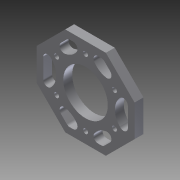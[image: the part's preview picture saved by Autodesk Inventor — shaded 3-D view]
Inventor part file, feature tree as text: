
AUTODESK INVENTOR PART (.ipt)
format: ipt  version: 2012 (Build 160160000, 160)  size: 206,336 bytes
history: native  units: in
note: dims shown in document units (in); Inventor stores cm internally (conversion verified against a paired STEP export)
features: sketch x1, extrude x1, fillet x1
ambient origin geometry x8: Origin, YZ Plane, XZ Plane, XY Plane, X Axis, Y Axis, Z Axis, Center Point
bodies: Solid1 (feature_tree)
feature tree (3):
  sketch  "Sketch1"  dims[d0=2.75in d1=2.5in d2=1.375in d3=1.25in d6=45.0deg d7=45.0deg d8=45.0deg d10=0.136in d11=0.938in d18=1.125in d19=1.25in d20=2.3622in d22=360.0deg d24=0.1875in d25=0.1875in d26=0.1875in d27=0.1875in d28=0.1875in d29=0.1875in d30=0.1875in d32=0.1875in d33=0.5in d34=0.25in d35=0.0in d38=0.125in d39=0.125in]
  extrude  "Extrusion1"  Depth=2.5in
  fillet  "Fillet1"  Radius=1.375in
